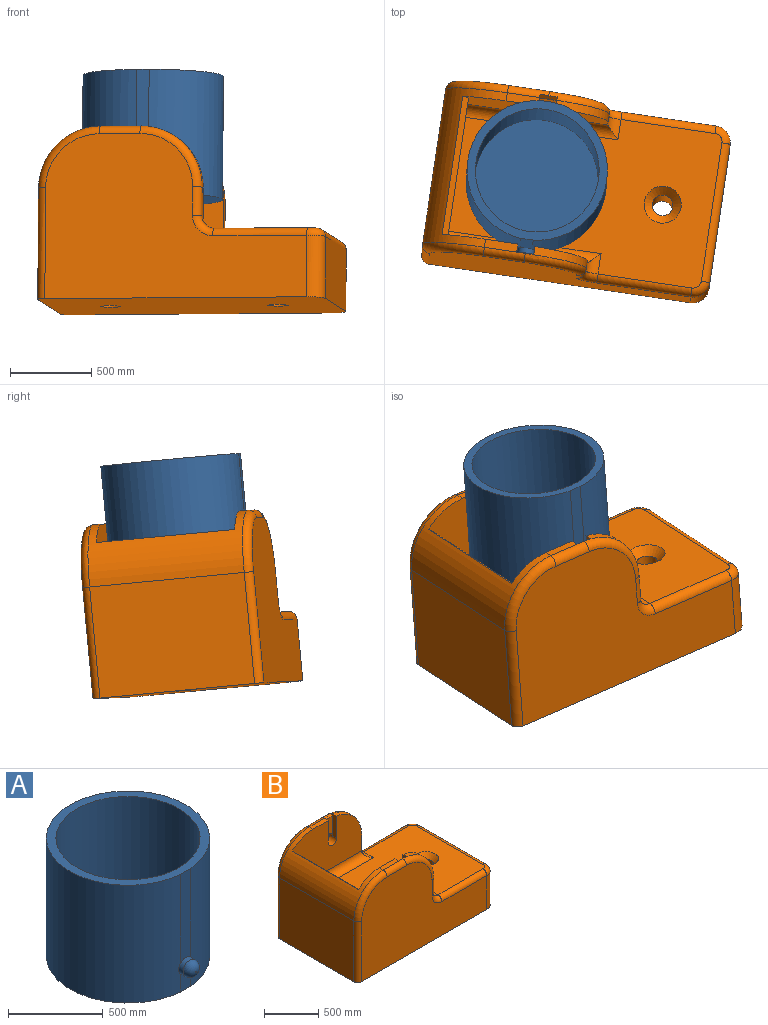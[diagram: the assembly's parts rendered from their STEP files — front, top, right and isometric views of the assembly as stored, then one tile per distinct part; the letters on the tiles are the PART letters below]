
ASSEMBLY  parts=2 mates=1
PART A: 16 faces, bbox 863.6x1016.4x762 mm
  f0: cylinder r=431.8mm len=860.23mm, axis (0,0,-1), area 974369.6mm2, adj f2,f3,f4,f5,f8,f9,f10,f11
  f1: cylinder r=431.8mm len=860.23mm, axis (0,0,-1), area 974369.6mm2, adj f2,f3,f4,f5,f8,f9,f10,f11
  f2: plane 118.8x76.2mm, normal (0,-1,0), area 8144.1mm2, adj f0,f1,f5,f11
  f3: plane 118.8x76.2mm, normal (0,1,0), area 8144.1mm2, adj f0,f1,f5,f10
  f4: plane 863.6x860.23mm, normal (0,0,1), area 129545.9mm2, adj f0,f1,f6,f8,f9
  f5: plane 863.6x860.23mm, normal (0,0,-1), area 585582.7mm2, adj f0,f1,f2,f3
  f6: cylinder r=381mm len=762mm, axis (0,0,1), area 1702537.1mm2, adj f4,f7
  f7: plane 762x762mm, normal (0,0,1), area 456036.7mm2, adj f6
  f8: plane 576x76.2mm, normal (0,1,0), area 42982.8mm2, adj f0,f1,f4,f10
  f9: plane 576x76.2mm, normal (0,-1,0), area 42982.8mm2, adj f0,f1,f4,f11
  f10: cylinder r=50.8mm len=101.6mm, axis (0,-1,0), area 9041.9mm2, adj f0,f1,f3,f8,f13
  f11: cylinder r=50.8mm len=101.6mm, axis (0,1,0), area 10258mm2, adj f0,f1,f2,f9,f15
  f12: plane 5.08x5.08mm, normal (0,1,0), area 20.3mm2, adj f13
  f13: torus R=2.54mm, axis (0,1,0), area 15843.5mm2, adj f10,f12
  f14: plane 5.08x5.08mm, normal (0,-1,0), area 20.3mm2, adj f15
  f15: torus R=2.54mm, axis (0,-1,0), area 15843.5mm2, adj f11,f14
PART B: 60 faces, bbox 1817.8x1083.5x1098.2 mm
  f0: cylinder r=381mm len=377.25mm, axis (0,-1,0), area 27683.8mm2, adj f9,f10,f27,f48
  f1: plane 200.66x50.8mm, normal (0,0,1), area 10193.5mm2, adj f12,f14,f21,f47
  f2: cylinder r=381mm len=377.25mm, axis (0,-1,0), area 27683.8mm2, adj f12,f13,f22,f49
  f3: plane 1600.2x965.2mm, normal (0,0,1), area 1216158mm2, adj f33,f34,f35,f36,f37,f40,f41,f54
  f4: plane 965.2x685.8mm, normal (-1,0,0), area 661934.2mm2, adj f8,f14,f42,f43
  f5: plane 1625.6x1016mm, normal (0,-1,0), area 1156662mm2, adj f8,f38,f42,f44,f46,f48,f50,f52
  f6: plane 863.6x381mm, normal (1,0,0), area 329031.6mm2, adj f8,f38,f39,f58
  f7: plane 1625.6x1016mm, normal (0,1,0), area 1156662mm2, adj f8,f39,f43,f45,f47,f49,f51,f53
  f8: plane 1778x1066.8mm, normal (0,0,-1), area 1865896.9mm2, adj f4,f5,f6,f7,f19,f20,f38,f39
  f9: plane 965.2x558.8mm, normal (0,1,0), area 450562.2mm2, adj f0,f10,f11,f14,f26,f27,f30,f31
  f10: plane 177.8x50.8mm, normal (1,0,0), area 9032.2mm2, adj f0,f9,f33,f50
  f11: plane 200.66x50.8mm, normal (0,0,1), area 10193.5mm2, adj f9,f14,f26,f46
  f12: plane 965.2x558.8mm, normal (0,-1,0), area 450673.5mm2, adj f1,f2,f13,f14,f17,f21,f22,f30
  f13: plane 177.8x50.8mm, normal (1,0,0), area 9032.2mm2, adj f2,f12,f34,f51
  f14: cylinder r=381mm len=965.2mm, axis (0,1,0), area 319225.7mm2, adj f1,f4,f9,f11,f12,f32,f44,f45
  f15: cylinder r=53.34mm len=106.68mm, axis (0,1,0), area 12769mm2, adj f16,f28,f29
  f16: plane 106.68x106.68mm, normal (0,1,0), area 8938.3mm2, adj f15
  f17: cylinder r=53.34mm len=106.68mm, axis (0,-1,0), area 21281.7mm2, adj f12,f18,f21,f22,f23
  f18: plane 106.68x106.68mm, normal (0,-1,0), area 8938.3mm2, adj f17
  f19: cylinder r=63.5mm len=381mm, axis (0,0,1), area 152012.2mm2, adj f8,f41
  f20: cylinder r=63.5mm len=381mm, axis (0,0,1), area 152012.2mm2, adj f8,f40
  f21: plane 254x71.7mm, normal (1,0,0), area 13184.9mm2, adj f1,f12,f17,f23,f25,f47
  f22: plane 250.25x71.7mm, normal (-1,0,0), area 12997.2mm2, adj f2,f12,f17,f23,f24,f49
  f23: plane 228.6x106.68mm, normal (0,-1,0), area 19846.5mm2, adj f17,f21,f22,f24,f25
  f24: cone r=355.6mm half-angle=45deg, axis (0,1,0), area 1582.3mm2, adj f22,f23,f25,f49
  f25: plane 53.34x20.9mm, normal (0,-0.71,0.71), area 1576.7mm2, adj f21,f23,f24,f47
  f26: plane 255.04x50.8mm, normal (1,0,0), area 12956.2mm2, adj f9,f11,f28,f29,f59
  f27: plane 251.29x50.8mm, normal (-1,0,0), area 12765.6mm2, adj f0,f9,f28,f29,f59
  f28: plane 254x106.68mm, normal (0,1,0), area 22561mm2, adj f15,f26,f27,f46,f48
  f29: plane 106.68x54.38mm, normal (0,1,0), area 111.2mm2, adj f15,f26,f27,f59
  f30: plane 863.6x177.8mm, normal (1,0,0), area 153548.1mm2, adj f9,f12,f31,f37
  f31: cylinder r=330.34mm len=863.6mm, axis (0,1,0), area 225603.5mm2, adj f9,f12,f30,f32
  f32: plane 863.6x37.23mm, normal (0.68,0,0.73), area 43870.9mm2, adj f9,f12,f14,f31
  f33: cylinder r=76.2mm len=127mm, axis (0,1,0), area 9394.8mm2, adj f3,f10,f35,f52
  f34: cylinder r=76.2mm len=127mm, axis (0,1,0), area 9394.8mm2, adj f3,f13,f36,f53
  f35: cylinder r=76.2mm len=1041.4mm, axis (-1,0,0), area 115529.3mm2, adj f3,f9,f33,f37
  f36: cylinder r=76.2mm len=1041.4mm, axis (1,0,0), area 115529.3mm2, adj f3,f12,f34,f37
  f37: cylinder r=76.2mm len=863.6mm, axis (0,1,0), area 96739.7mm2, adj f3,f30,f35,f36
  f38: cylinder r=101.6mm len=381mm, axis (0,0,-1), area 60804.9mm2, adj f5,f6,f8,f56
  f39: cylinder r=101.6mm len=381mm, axis (0,0,1), area 60804.9mm2, adj f6,f7,f8,f57
  f40: cone r=63.5mm half-angle=45deg, axis (0,0,1), area 40129.2mm2, adj f3,f20
  f41: cone r=63.5mm half-angle=45deg, axis (0,0,1), area 40129.2mm2, adj f3,f19
  f42: cylinder r=50.8mm len=685.8mm, axis (0,0,1), area 54724.4mm2, adj f4,f5,f8,f44
  f43: cylinder r=50.8mm len=685.8mm, axis (0,0,-1), area 54724.4mm2, adj f4,f7,f8,f45
  f44: torus R=330.2mm, axis (0,1,0), area 45442.2mm2, adj f5,f14,f42,f46
  f45: torus R=330.2mm, axis (0,1,0), area 45442.2mm2, adj f7,f14,f43,f47
  f46: cylinder r=50.8mm len=254mm, axis (-1,0,0), area 20268.3mm2, adj f5,f11,f28,f44,f48
  f47: cylinder r=50.8mm len=254mm, axis (1,0,0), area 19119.3mm2, adj f1,f7,f21,f25,f45,f49
  f48: torus R=330.2mm, axis (0,1,0), area 45442.2mm2, adj f0,f5,f28,f46,f50
  f49: torus R=330.2mm, axis (0,1,0), area 44289.4mm2, adj f2,f7,f22,f24,f47,f51
  f50: cylinder r=50.8mm len=177.8mm, axis (0,0,-1), area 14187.8mm2, adj f5,f10,f48,f52
  f51: cylinder r=50.8mm len=177.8mm, axis (0,0,-1), area 14187.8mm2, adj f7,f13,f49,f53
  f52: torus R=127mm, axis (0,1,0), area 11865mm2, adj f5,f33,f50,f54
  f53: torus R=127mm, axis (0,1,0), area 11865mm2, adj f7,f34,f51,f55
  f54: cylinder r=50.8mm len=584.2mm, axis (-1,0,0), area 46617.1mm2, adj f3,f5,f52,f56
  f55: cylinder r=50.8mm len=584.2mm, axis (1,0,0), area 46617.1mm2, adj f3,f7,f53,f57
  f56: torus R=50.8mm, axis (0,0,1), area 10421.1mm2, adj f3,f38,f54,f58
  f57: torus R=50.8mm, axis (0,0,1), area 10421.1mm2, adj f3,f39,f55,f58
  f58: cylinder r=50.8mm len=863.6mm, axis (0,-1,0), area 68912.2mm2, adj f3,f6,f56,f57
  f59: cylinder r=53.34mm len=106.68mm, axis (0,-1,0), area 8512.7mm2, adj f9,f26,f27,f29
PLACE A rot(axis=(-0.54,0.01,-0.84),10deg) t=(23.15,155.3,650.05)mm
PLACE B rot(axis=(-0.54,0,-0.84),10deg) t=(-107.85,-131.31,14.53)mm
MATE revolute A.f10 <-> B.f15  axis (0.15,0.98,-0.09) through (43.44,660.37,755.83)mm
